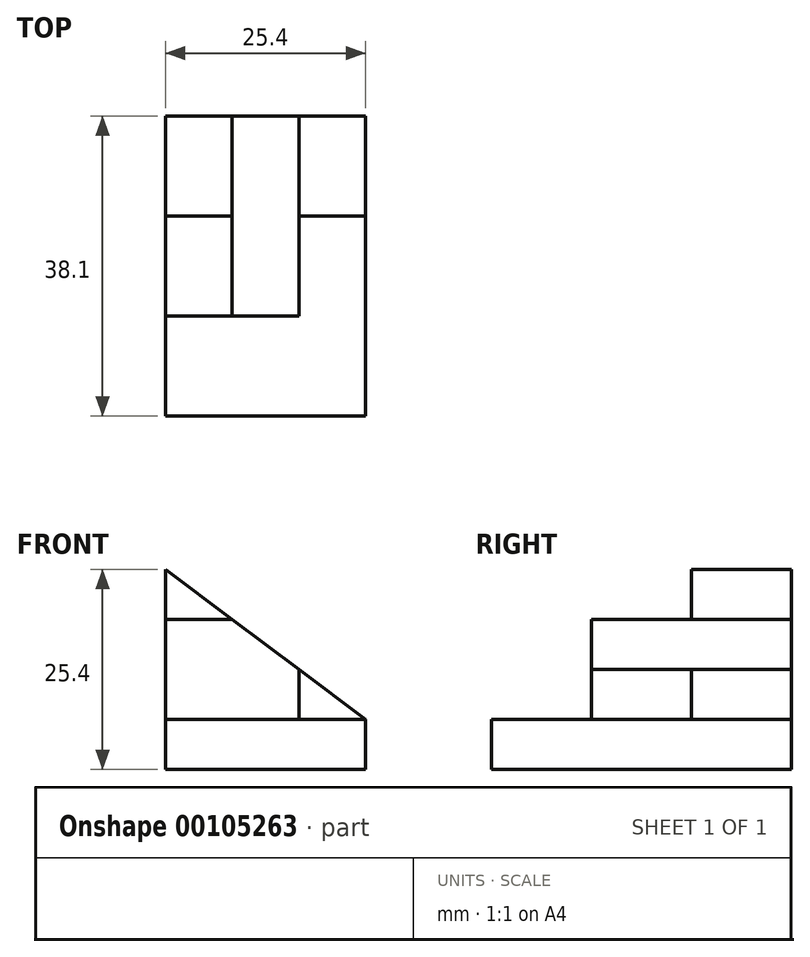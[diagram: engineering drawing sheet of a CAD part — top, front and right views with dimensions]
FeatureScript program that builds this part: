
annotation { "Feature Type Name" : "Feature", "Feature Type Description" : "" }
export const myFeature = defineFeature(function(context is Context, id is Id, definition is map)
    precondition{}
    {
        {
            var Q0;
            Q0=qCreatedBy(makeId("Front.planeOp"),FACE);
            var sketch = newSketch(context, id + "F0", { "sketchPlane" : qUnion([Q0])});
            skLineSegment(sketch, "E0.bottom", {"start": v(0, 0) * mm, "end": v(25.4, 0) * mm});
            skLineSegment(sketch, "E0.top", {"start": v(0, 6.35) * mm, "end": v(25.4, 6.35) * mm});
            skLineSegment(sketch, "E0.left", {"start": v(0, 0) * mm, "end": v(0, 6.35) * mm});
            skLineSegment(sketch, "E0.right", {"start": v(25.4, 0) * mm, "end": v(25.4, 6.35) * mm});
            skLineSegment(sketch, "E1", {"start": v(0, 6.35) * mm, "end": v(0, 25.4) * mm});
            skLineSegment(sketch, "E2", {"start": v(0, 25.4) * mm, "end": v(25.4, 6.35) * mm});
            skLineSegment(sketch, "E3", {"start": v(16.94, 6.35) * mm, "end": v(16.94, 12.7) * mm});
            skLineSegment(sketch, "E4", {"start": v(0, 19.05) * mm, "end": v(8.47, 19.05) * mm});
            skSolve(sketch);
        }
        {
            var Q0;
            Q0=makeQuery(id+"F0.imprint","IMPRINT",FACE,{"disambiguationData":[TD([[makeQuery(id+"F0.imprint","IMPRINT",EDGE,{"derivedFrom":sQuery(id+"F0.wireOp",EDGE,"E0.bottom")}),1.0]])]});
            extrude(context, id + "F1", {"entities" : qUnion([Q0]), "depth" : 38.1 * mm});
        }
        {
            var Q0;
            {var subQ3=sQuery(id+"F0.wireOp",EDGE,"E4");Q0=makeQuery(id+"F0.imprint","IMPRINT",FACE,{"disambiguationData":[TD([[makeQuery(id+"F0.imprint","IMPRINT",EDGE,{"derivedFrom":subQ3}),1.0]])]});}
            var Q1;
            {var subQ3=sQuery(id+"F0.wireOp",EDGE,"E3");Q1=makeQuery(id+"F0.imprint","IMPRINT",FACE,{"disambiguationData":[TD([[makeQuery(id+"F0.imprint","IMPRINT",EDGE,{"derivedFrom":subQ3}),-1.0]])]});}
            extrude(context, id + "F2", {"entities" : qUnion([Q0, Q1]), "operationType" : NewBodyOperationType.ADD, "depth" : 12.7 * mm});
        }
        {
            var Q0;
            {var subQ0=sQuery(id+"F0.wireOp",EDGE,"E3");Q0=makeQuery(id+"F0.imprint","IMPRINT",FACE,{"disambiguationData":[TD([[makeQuery(id+"F0.imprint","IMPRINT",EDGE,{"derivedFrom":subQ0}),1.0]])]});}
            extrude(context, id + "F3", {"entities" : qUnion([Q0]), "depth" : 25.4 * mm});
        }
    });
